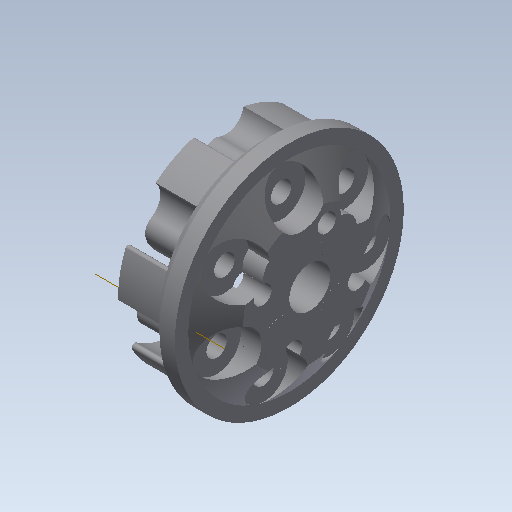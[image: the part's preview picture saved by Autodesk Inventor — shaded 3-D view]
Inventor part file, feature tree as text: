
AUTODESK INVENTOR PART (.ipt)
format: ipt  version: 2020 (Build 240168000, 168)  size: 737,792 bytes
history: native  units: in
note: dims shown in document units (in); Inventor stores cm internally (conversion verified against a paired STEP export)
features: other x4, sketch x4, extrude x2, plane x2, mirror x1
ambient origin geometry x8: Origin, YZ Plane, XZ Plane, XY Plane, X Axis, Y Axis, Z Axis, Center Point
bodies: Solid1 (feature_tree)
feature tree (13):
  other  "Mecanum Adaptor 1.3.ipt"
  extrude  "Extrusion1"  Depth=0.217in TaperAngle=0.0deg
  extrude  "Extrusion2"  Depth=0.1406in
  mirror  "Mirror1"
  other  "Solid1::Mecanum Adaptor 1.3.ipt"
  other  "TaggingFeature1"
  sketch  "Sketch6"  dims[d0=0.3937in]
  sketch  "Sketch11"  dims[d4=0.4724in d5=0.0in d6=0.0787in d7=1.757in d8=1.6061in d9=0.0in d10=90.0deg d11=0.0in d12=90.0deg d13=0.1181in d14=0.0in d15=0.1575in d16=2.7559in d21=0.0in d23=0.0in d25=0.0in d26=0.1575in d27=0.0in d28=0.374in d29=2.7559in d33=0.0787in d34=0.0in d35=0.1378in d36=0.0in d38=0.0in d55=2.7559in d60=0.0in d61=0.2756in d62=0.7874in d64=0.446in d65=0.7874in d67=0.446in d70=0.0984in d71=0.0in d72=0.2638in d73=0.1575in d75=0.2638in d76=0.1575in d78=0.2638in d79=0.1575in d81=0.2638in d82=0.1575in d84=0.2638in d85=0.1575in d87=0.2638in d88=0.1575in d90=0.2638in d91=0.1575in d93=0.1575in d2=360.0deg d18=360.0deg d31=360.0deg d57=360.0deg d1=0.217in d3=0.0in]
  plane  "Work Plane1"
  plane  "Work Plane2"
  other  "Work Axis1"
  sketch  "Sketch18"  dims[d19=0.1406in d20=0.1406in]
  sketch  "Sketch19"  dims[d22=0.1406in d24=0.1406in d30=0.7795in d32=0.0in]
